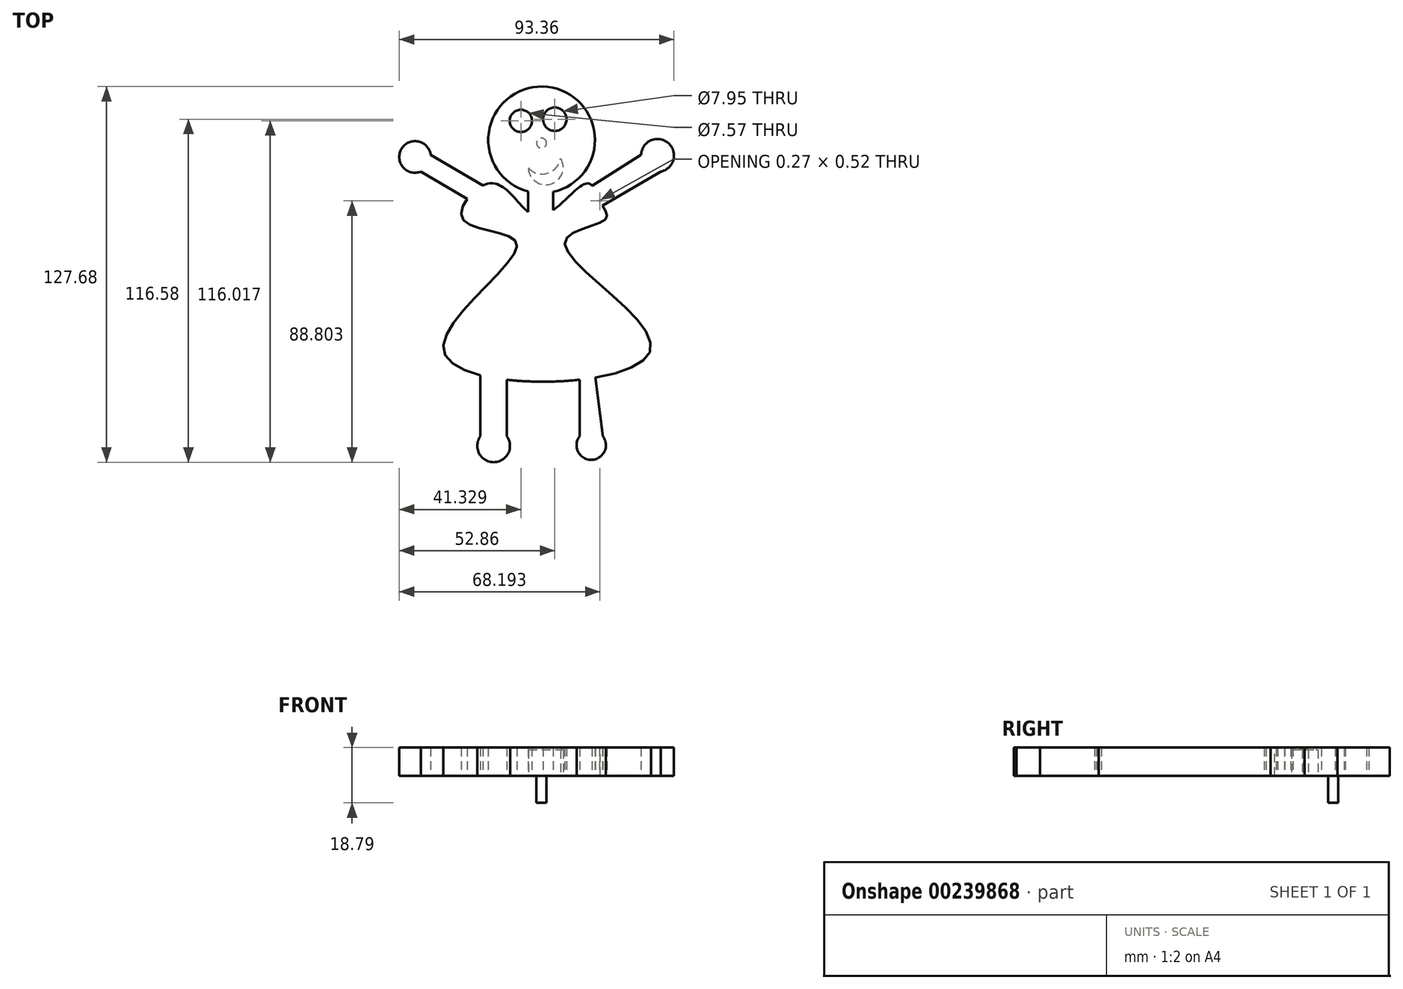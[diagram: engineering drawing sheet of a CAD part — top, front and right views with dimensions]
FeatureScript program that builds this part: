
annotation { "Feature Type Name" : "Feature", "Feature Type Description" : "" }
export const myFeature = defineFeature(function(context is Context, id is Id, definition is map)
    precondition{}
    {
        {
            var Q0;
            Q0=qCreatedBy(makeId("Top.planeOp"),FACE);
            var sketch = newSketch(context, id + "F0", { "sketchPlane" : qUnion([Q0])});
            skArc(sketch, "E0", {"start": v(3.94, 20.97) * mm, "mid": v(0.32, 56.8) * mm, "end": v(-4.56, 21.12) * mm});
            skLineSegment(sketch, "E1.left", {"start": v(-4.56, 21.12) * mm, "end": v(-4.56, 14.2) * mm});
            skLineSegment(sketch, "E1.right", {"start": v(3.94, 21.12) * mm, "end": v(3.94, 14.76) * mm});
            skLineSegment(sketch, "E2", {"start": v(-19.91, 23.2) * mm, "end": v(-37.68, 33.6) * mm});
            skLineSegment(sketch, "E3", {"start": v(-37.68, 33.6) * mm, "end": v(-41.03, 27.9) * mm});
            skLineSegment(sketch, "E4", {"start": v(-41.03, 27.9) * mm, "end": v(-25.26, 18.66) * mm});
            skLineSegment(sketch, "E5", {"start": v(20.73, 16.34) * mm, "end": v(40.5, 27.9) * mm});
            skLineSegment(sketch, "E6", {"start": v(40.5, 27.9) * mm, "end": v(33.82, 33.6) * mm});
            skLineSegment(sketch, "E7", {"start": v(33.82, 33.6) * mm, "end": v(17.17, 23.1) * mm});
            skLineSegment(sketch, "E8.trimOffspring", {"start": v(-4.56, -43.4) * mm, "end": v(-4.56, -44.01) * mm});
            skLineSegment(sketch, "E9.trimOffspring", {"start": v(3.94, -43.45) * mm, "end": v(3.94, -44.01) * mm});
            skPoint(sketch, "E10.1.internal.snap0", {"position": v(-21.12, 23.9) * mm});
            skPoint(sketch, "E10.8.internal.snap0", {"position": v(-4.56, 17.66) * mm});
            skPoint(sketch, "E10.9.internal.snap0", {"position": v(-21.12, 23.9) * mm});
            skFitSpline(sketch, "E10", {"points": [v(-4.56, 14.2) * mm, v(-17.44, 23.9) * mm, v(-26.72, 11.67) * mm, v(-8.44, 3.23) * mm, v(-32.9, -34.17) * mm, v(36.84, -33.33) * mm, v(7.87, 3.52) * mm, v(21.65, 11.67) * mm, v(19.97, 17.66) * mm, v(15.75, 23.9) * mm, v(3.94, 14.76) * mm, v(-4.56, 14.2) * mm]});
            skArc(sketch, "E11", {"start": v(-37.68, 33.6) * mm, "mid": v(-47.63, 35.6) * mm, "end": v(-41.03, 27.9) * mm});
            skArc(sketch, "E12", {"start": v(40.5, 27.9) * mm, "mid": v(43.04, 37.63) * mm, "end": v(33.82, 33.6) * mm});
            skLineSegment(sketch, "E13", {"start": v(-20.76, -41.28) * mm, "end": v(-20.76, -62.01) * mm});
            skLineSegment(sketch, "E14", {"start": v(-20.76, -62.01) * mm, "end": v(-11.81, -62.01) * mm});
            skLineSegment(sketch, "E15", {"start": v(-11.81, -62.01) * mm, "end": v(-11.81, -42.84) * mm});
            skLineSegment(sketch, "E16", {"start": v(12.94, -42.84) * mm, "end": v(12.94, -62.01) * mm});
            skLineSegment(sketch, "E17", {"start": v(12.94, -62.01) * mm, "end": v(20.81, -62.01) * mm});
            skLineSegment(sketch, "E18", {"start": v(20.81, -62.01) * mm, "end": v(18.34, -42.1) * mm});
            skArc(sketch, "E19", {"start": v(-20.76, -62.01) * mm, "mid": v(-16.29, -70.88) * mm, "end": v(-11.81, -62.01) * mm});
            skArc(sketch, "E20", {"start": v(12.94, -62.01) * mm, "mid": v(16.88, -70.07) * mm, "end": v(20.81, -62.01) * mm});
            skLineSegment(sketch, "E21", {"start": v(-19.91, 23.2) * mm, "end": v(-25.26, 18.66) * mm});
            skLineSegment(sketch, "E22", {"start": v(17.17, 23.1) * mm, "end": v(19.97, 17.66) * mm});
            skLineSegment(sketch, "E23", {"start": v(-20.76, -41.28) * mm, "end": v(-11.81, -42.84) * mm});
            skLineSegment(sketch, "E24", {"start": v(12.94, -42.84) * mm, "end": v(18.34, -42.1) * mm});
            skSolve(sketch);
        }
        {
            var Q0;
            Q0 = qSketchRegion(id + "F0", true);
            extrude(context, id + "F1", {"entities" : qUnion([Q0]), "depth" : 9.65 * mm});
        }
        {
            var Q0;
            Q0=qCreatedBy(makeId("Top.planeOp"),FACE);
            var sketch = newSketch(context, id + "F2", { "sketchPlane" : qUnion([Q0])});
            skCircle(sketch, "E25", {"center": v(-7.03, 45.14) * mm, "radius": 3.78 * mm});
            skCircle(sketch, "E26", {"center": v(4.5, 45.7) * mm, "radius": 3.98 * mm});
            skSolve(sketch);
        }
        {
            var Q0;
            Q0 = qSketchRegion(id + "F2", true);
            extrude(context, id + "F3", {"entities" : qUnion([Q0]), "operationType" : NewBodyOperationType.REMOVE, "depth" : 44.7 * mm});
        }
        {
            var Q0;
            Q0=qCreatedBy(makeId("Top.planeOp"),FACE);
            var sketch = newSketch(context, id + "F4", { "sketchPlane" : qUnion([Q0])});
            skArc(sketch, "E27", {"start": v(-4.5, 29.1) * mm, "mid": v(2.05, 27.32) * mm, "end": v(6.47, 32.48) * mm});
            skArc(sketch, "E28", {"start": v(-4.5, 29.1) * mm, "mid": v(3.17, 23.68) * mm, "end": v(6.47, 32.48) * mm});
            skSolve(sketch);
        }
        {
            var Q0;
            Q0 = qSketchRegion(id + "F4", true);
            extrude(context, id + "F5", {"entities" : qUnion([Q0]), "operationType" : NewBodyOperationType.REMOVE, "depth" : 8.9 * mm});
        }
        {
            var Q0;
            Q0=qCreatedBy(makeId("Top.planeOp"),FACE);
            var sketch = newSketch(context, id + "F6", { "sketchPlane" : qUnion([Q0])});
            skCircle(sketch, "E29", {"center": v(0, 37.55) * mm, "radius": 1.7 * mm});
            skSolve(sketch);
        }
        {
            var Q0;
            Q0 = qSketchRegion(id + "F6", true);
            extrude(context, id + "F7", {"entities" : qUnion([Q0]), "operationType" : NewBodyOperationType.ADD, "oppositeDirection" : true, "depth" : 9.14 * mm});
        }
    });
